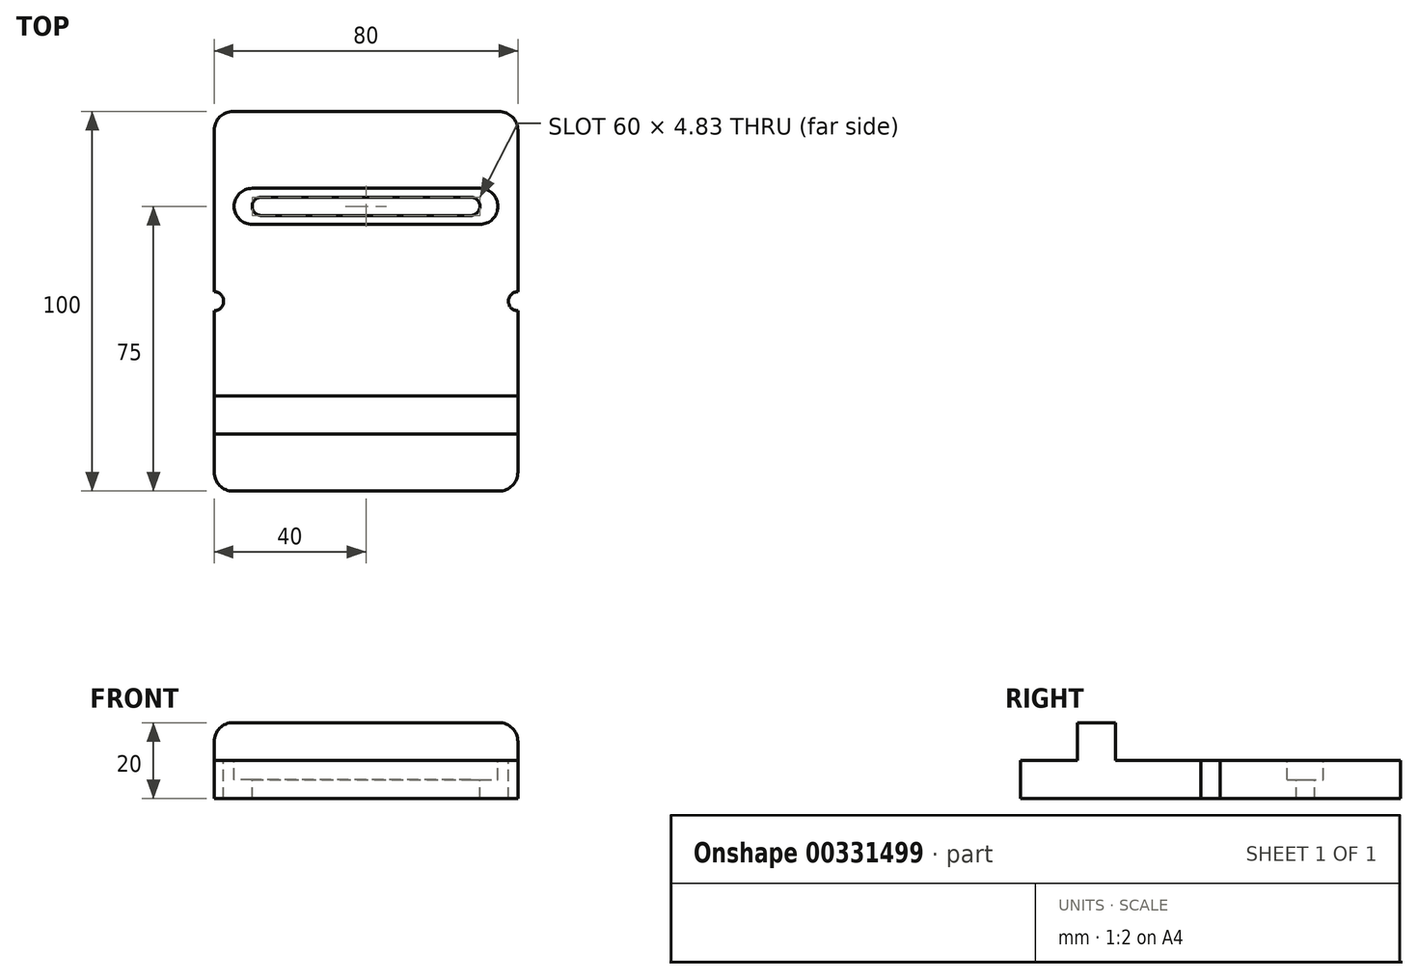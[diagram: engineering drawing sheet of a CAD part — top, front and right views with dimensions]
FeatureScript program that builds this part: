
annotation { "Feature Type Name" : "Feature", "Feature Type Description" : "" }
export const myFeature = defineFeature(function(context is Context, id is Id, definition is map)
    precondition{}
    {
        {
            assignVariable(context, id + "F0", {"name" : "radius", "anyValue" : 5});
        }
        {
            assignVariable(context, id + "F1", {"name" : "thickness", "anyValue" : 10});
        }
        {
            var Q0;
            Q0=qCreatedBy(makeId("Top.planeOp"),FACE);
            var sketch = newSketch(context, id + "F2", { "sketchPlane" : qUnion([Q0])});
            skLineSegment(sketch, "E0.bottom", {"start": v(-35, 50) * mm, "end": v(35, 50) * mm});
            skLineSegment(sketch, "E0.top", {"start": v(-35, -50) * mm, "end": v(35, -50) * mm});
            skLineSegment(sketch, "E0.left", {"start": v(-40, 45) * mm, "end": v(-40, -45) * mm});
            skLineSegment(sketch, "E0.right", {"start": v(40, 45) * mm, "end": v(40, -45) * mm});
            skPoint(sketch, "E1.visualSharp", {"position": v(-40, 50) * mm});
            skArc(sketch, "E1.filletArc", {"start": v(-35, 50) * mm, "mid": v(-38.54, 48.54) * mm, "end": v(-40, 45) * mm});
            skPoint(sketch, "E2.visualSharp", {"position": v(40, 50) * mm});
            skArc(sketch, "E2.filletArc", {"start": v(40, 45) * mm, "mid": v(38.54, 48.54) * mm, "end": v(35, 50) * mm});
            skPoint(sketch, "E3.visualSharp", {"position": v(40, -50) * mm});
            skArc(sketch, "E3.filletArc", {"start": v(35, -50) * mm, "mid": v(38.54, -48.54) * mm, "end": v(40, -45) * mm});
            skPoint(sketch, "E4.visualSharp", {"position": v(-40, -50) * mm});
            skArc(sketch, "E4.filletArc", {"start": v(-40, -45) * mm, "mid": v(-38.54, -48.54) * mm, "end": v(-35, -50) * mm});
            skSolve(sketch);
        }
        {
            var Q0;
            Q0 = qSketchRegion(id + "F2", true);
            extrude(context, id + "F3", {"entities" : qUnion([Q0]), "depth" : (getVariable(context, 'thickness')) * mm});
        }
        {
            var Q0;
            Q0=makeQuery(id+"F3.opExtrude","CAP_FACE",FACE,{"disambiguationData":[OSD([sQuery(id+"F2.wireOp",EDGE,"E0.bottom"),sQuery(id+"F2.wireOp",EDGE,"E0.top"),sQuery(id+"F2.wireOp",EDGE,"E0.left"),sQuery(id+"F2.wireOp",EDGE,"E0.right"),sQuery(id+"F2.wireOp",EDGE,"E1.filletArc"),sQuery(id+"F2.wireOp",EDGE,"E2.filletArc"),sQuery(id+"F2.wireOp",EDGE,"E3.filletArc"),sQuery(id+"F2.wireOp",EDGE,"E4.filletArc")])],"isStart":false});
            var sketch = newSketch(context, id + "F4", { "sketchPlane" : qUnion([Q0])});
            skLineSegment(sketch, "E5.bottom", {"start": v(-40, -25) * mm, "end": v(40, -25) * mm});
            skLineSegment(sketch, "E5.top", {"start": v(-40, -35) * mm, "end": v(40, -35) * mm});
            skLineSegment(sketch, "E5.left", {"start": v(-40, -25) * mm, "end": v(-40, -35) * mm});
            skLineSegment(sketch, "E5.right", {"start": v(40, -25) * mm, "end": v(40, -35) * mm});
            skSolve(sketch);
        }
        {
            var Q0;
            Q0 = qSketchRegion(id + "F4", true);
            extrude(context, id + "F5", {"entities" : qUnion([Q0]), "operationType" : NewBodyOperationType.ADD, "depth" : 10 * mm});
        }
        {
            var Q0;
            Q0=makeQuery(id+"F5.opExtrude","CAP_EDGE",EDGE,{"disambiguationData":[OSD([sQuery(id+"F4.wireOp",EDGE,"E5.right")])],"isStart":false});
            var Q1;
            Q1=makeQuery(id+"F5.opExtrude","CAP_EDGE",EDGE,{"disambiguationData":[OSD([sQuery(id+"F4.wireOp",EDGE,"E5.left")])],"isStart":false});
            fillet(context, id + "F6", {"entities" : qUnion([Q0, Q1]), "radius" : (getVariable(context, 'radius')) * mm, "tangentPropagation" : true, "allowEdgeOverflow" : false});
        }
        {
            var Q0;
            {var subQ0=sQuery(id+"F2.wireOp",EDGE,"E1.filletArc");var subQ1=sQuery(id+"F2.wireOp",EDGE,"E0.left");var subQ2=sQuery(id+"F2.wireOp",EDGE,"E0.right");var subQ3=sQuery(id+"F2.wireOp",EDGE,"E0.bottom");var subQ4=sQuery(id+"F2.wireOp",EDGE,"E2.filletArc");Q0=makeQuery(id+"F5.boolean.opBoolean","SPLIT",FACE,{"disambiguationData":[TD([makeQuery(id+"F3.opExtrude","SWEPT_FACE",FACE,{"disambiguationData":[OSD([subQ3])]})])],"derivedFrom":makeQuery(id+"F3.opExtrude","CAP_FACE",FACE,{"disambiguationData":[OSD([subQ3,sQuery(id+"F2.wireOp",EDGE,"E0.top"),subQ1,subQ2,subQ0,subQ4,sQuery(id+"F2.wireOp",EDGE,"E3.filletArc"),sQuery(id+"F2.wireOp",EDGE,"E4.filletArc")])],"isStart":false})});}
            var sketch = newSketch(context, id + "F7", { "sketchPlane" : qUnion([Q0])});
            skLineSegment(sketch, "E6.bottom", {"start": v(-27.59, 27.41) * mm, "end": v(27.59, 27.41) * mm});
            skLineSegment(sketch, "E6.top", {"start": v(-27.59, 22.59) * mm, "end": v(27.59, 22.59) * mm});
            skLineSegment(sketch, "E6.left", {"start": v(-30, 25) * mm, "end": v(-30, 25) * mm});
            skLineSegment(sketch, "E6.right", {"start": v(30, 25) * mm, "end": v(30, 25) * mm});
            skPoint(sketch, "E7.visualSharp", {"position": v(30, 27.41) * mm});
            skArc(sketch, "E7.filletArc", {"start": v(30, 25) * mm, "mid": v(29.3, 26.7) * mm, "end": v(27.59, 27.41) * mm});
            skPoint(sketch, "E8.visualSharp", {"position": v(30, 22.59) * mm});
            skArc(sketch, "E8.filletArc", {"start": v(27.59, 22.59) * mm, "mid": v(29.3, 23.3) * mm, "end": v(30, 25) * mm});
            skPoint(sketch, "E9.visualSharp", {"position": v(-30, 27.41) * mm});
            skArc(sketch, "E9.filletArc", {"start": v(-27.59, 27.41) * mm, "mid": v(-29.3, 26.7) * mm, "end": v(-30, 25) * mm});
            skPoint(sketch, "E10.visualSharp", {"position": v(-30, 22.59) * mm});
            skArc(sketch, "E10.filletArc", {"start": v(-30, 25) * mm, "mid": v(-29.3, 23.3) * mm, "end": v(-27.59, 22.59) * mm});
            skLineSegment(sketch, "E11", {"start": v(-45.69, 25) * mm, "end": v(55.56, 25) * mm, "construction": true});
            skSolve(sketch);
        }
        {
            var Q0;
            Q0 = qSketchRegion(id + "F7", true);
            extrude(context, id + "F8", {"entities" : qUnion([Q0]), "operationType" : NewBodyOperationType.REMOVE, "endBound" : BoundingType.UP_TO_NEXT, "oppositeDirection" : true, "depth" : 25 * mm});
        }
        {
            var Q0;
            {var subQ0=sQuery(id+"F2.wireOp",EDGE,"E1.filletArc");var subQ1=sQuery(id+"F2.wireOp",EDGE,"E0.left");var subQ2=sQuery(id+"F2.wireOp",EDGE,"E0.right");var subQ3=sQuery(id+"F2.wireOp",EDGE,"E0.bottom");var subQ4=sQuery(id+"F2.wireOp",EDGE,"E2.filletArc");Q0=makeQuery(id+"F5.boolean.opBoolean","SPLIT",FACE,{"disambiguationData":[TD([makeQuery(id+"F3.opExtrude","SWEPT_FACE",FACE,{"disambiguationData":[OSD([subQ3])]})])],"derivedFrom":makeQuery(id+"F3.opExtrude","CAP_FACE",FACE,{"disambiguationData":[OSD([subQ3,sQuery(id+"F2.wireOp",EDGE,"E0.top"),subQ1,subQ2,subQ0,subQ4,sQuery(id+"F2.wireOp",EDGE,"E3.filletArc"),sQuery(id+"F2.wireOp",EDGE,"E4.filletArc")])],"isStart":false})});}
            var sketch = newSketch(context, id + "F9", { "sketchPlane" : qUnion([Q0])});
            skLineSegment(sketch, "E12.bottom", {"start": v(-30, 29.74) * mm, "end": v(30, 29.74) * mm});
            skLineSegment(sketch, "E12.top", {"start": v(-30, 20.26) * mm, "end": v(30, 20.26) * mm});
            skLineSegment(sketch, "E13", {"start": v(-42.97, 25) * mm, "end": v(45.93, 25) * mm, "construction": true});
            skArc(sketch, "E14", {"start": v(30, 20.26) * mm, "mid": v(34.74, 25) * mm, "end": v(30, 29.74) * mm});
            skArc(sketch, "E15", {"start": v(-30, 29.74) * mm, "mid": v(-34.74, 25) * mm, "end": v(-30, 20.26) * mm});
            skSolve(sketch);
        }
        {
            var Q0;
            Q0 = qSketchRegion(id + "F9", true);
            extrude(context, id + "F10", {"entities" : qUnion([Q0]), "operationType" : NewBodyOperationType.REMOVE, "oppositeDirection" : true, "depth" : ((getVariable(context, 'thickness')) / 2) * mm});
        }
        {
            var Q0;
            {var subQ0=sQuery(id+"F2.wireOp",EDGE,"E1.filletArc");var subQ1=sQuery(id+"F2.wireOp",EDGE,"E0.left");var subQ2=sQuery(id+"F2.wireOp",EDGE,"E0.right");var subQ3=sQuery(id+"F2.wireOp",EDGE,"E0.bottom");var subQ4=sQuery(id+"F2.wireOp",EDGE,"E2.filletArc");Q0=makeQuery(id+"F5.boolean.opBoolean","SPLIT",FACE,{"disambiguationData":[TD([makeQuery(id+"F3.opExtrude","SWEPT_FACE",FACE,{"disambiguationData":[OSD([subQ3])]})])],"derivedFrom":makeQuery(id+"F3.opExtrude","CAP_FACE",FACE,{"disambiguationData":[OSD([subQ3,sQuery(id+"F2.wireOp",EDGE,"E0.top"),subQ1,subQ2,subQ0,subQ4,sQuery(id+"F2.wireOp",EDGE,"E3.filletArc"),sQuery(id+"F2.wireOp",EDGE,"E4.filletArc")])],"isStart":false})});}
            var sketch = newSketch(context, id + "F11", { "sketchPlane" : qUnion([Q0])});
            skArc(sketch, "E16", {"start": v(-40, 2.5) * mm, "mid": v(-37.5, 0) * mm, "end": v(-40, -2.5) * mm});
            skArc(sketch, "E17.MirrorCS", {"start": v(40, 2.5) * mm, "mid": v(37.5, 0) * mm, "end": v(40, -2.5) * mm});
            skLineSegment(sketch, "E18", {"start": v(-40, 2.5) * mm, "end": v(-40, -2.5) * mm});
            skLineSegment(sketch, "E19.MirrorCS", {"start": v(40, 2.5) * mm, "end": v(40, -2.5) * mm});
            skLineSegment(sketch, "E20", {"start": v(67.42, 0) * mm, "end": v(-54.54, 0) * mm, "construction": true});
            skSolve(sketch);
        }
        {
            var Q0;
            Q0 = qSketchRegion(id + "F11", true);
            extrude(context, id + "F12", {"entities" : qUnion([Q0]), "operationType" : NewBodyOperationType.REMOVE, "endBound" : BoundingType.UP_TO_NEXT, "oppositeDirection" : true, "depth" : 25 * mm});
        }
    });
